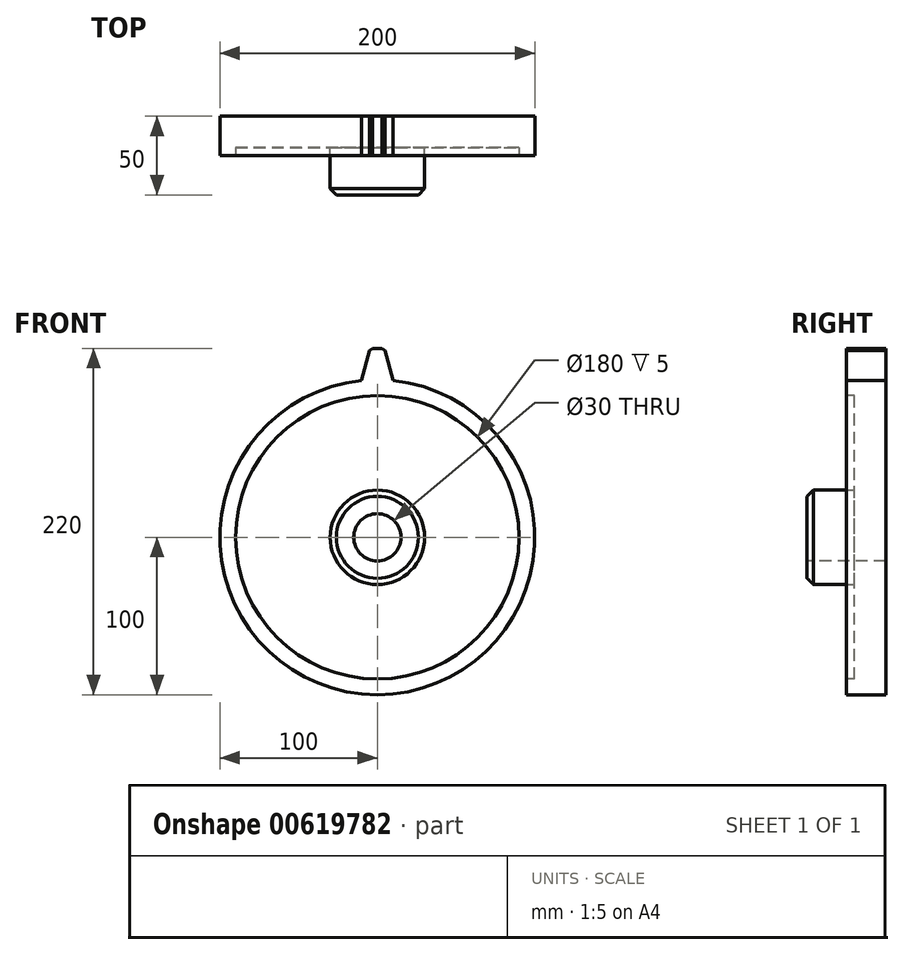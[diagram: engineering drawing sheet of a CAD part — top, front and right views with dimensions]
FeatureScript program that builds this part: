
annotation { "Feature Type Name" : "Feature", "Feature Type Description" : "" }
export const myFeature = defineFeature(function(context is Context, id is Id, definition is map)
    precondition{}
    {
        {
            var Q0;
            Q0=qCreatedBy(makeId("Front.planeOp"),FACE);
            var sketch = newSketch(context, id + "F0", { "sketchPlane" : qUnion([Q0])});
            skCircle(sketch, "E0", {"center": v(0, 0) * mm, "radius": 100 * mm});
            skSolve(sketch);
        }
        {
            var Q0;
            Q0=makeQuery(id+"F0.imprint","IMPRINT",FACE,{"disambiguationData":[TD([[makeQuery(id+"F0.imprint","IMPRINT",EDGE,{"derivedFrom":sQuery(id+"F0.wireOp",EDGE,"E0")}),1.0]])]});
            extrude(context, id + "F1", {"entities" : qUnion([Q0]), "depth" : 25 * mm, "offsetDistance" : 25 * mm});
        }
        {
            var Q0;
            Q0=makeQuery(id+"F1.opExtrude","CAP_FACE",FACE,{"disambiguationData":[OSD([sQuery(id+"F0.wireOp",EDGE,"E0")])],"isStart":false});
            var sketch = newSketch(context, id + "F2", { "sketchPlane" : qUnion([Q0])});
            skLineSegment(sketch, "E1", {"start": v(-10, 99.5) * mm, "end": v(10, 99.5) * mm});
            skLineSegment(sketch, "E2", {"start": v(10, 99.5) * mm, "end": v(4.5, 120) * mm});
            skLineSegment(sketch, "E3", {"start": v(4.5, 120) * mm, "end": v(-4.5, 120) * mm});
            skLineSegment(sketch, "E4", {"start": v(-4.5, 120) * mm, "end": v(-10, 99.5) * mm});
            skSolve(sketch);
        }
        {
            var Q0;
            {var subQ0=sQuery(id+"F2.wireOp",EDGE,"E2");Q0=makeQuery(id+"F2.imprint","IMPRINT",FACE,{"disambiguationData":[TD([[makeQuery(id+"F2.imprint","IMPRINT",EDGE,{"derivedFrom":subQ0}),1.0]])]});}
            var Q1;
            Q1=makeQuery(id+"F1.opExtrude","CAP_FACE",FACE,{"disambiguationData":[OSD([sQuery(id+"F0.wireOp",EDGE,"E0")])],"isStart":true});
            extrude(context, id + "F3", {"entities" : qUnion([Q0]), "operationType" : NewBodyOperationType.ADD, "endBound" : BoundingType.UP_TO_SURFACE, "oppositeDirection" : true, "depth" : 25 * mm, "endBoundEntityFace" : qUnion([Q1]), "offsetDistance" : 25 * mm});
        }
        {
            var Q0;
            Q0=makeQuery(id+"F3.opExtrude","SWEPT_EDGE",EDGE,{"disambiguationData":[OSD([sQuery(id+"F0.wireOp",EDGE,"E0"),sQuery(id+"F2.wireOp",EDGE,"E1"),sQuery(id+"F2.wireOp",EDGE,"E2")])]});
            var Q1;
            Q1=makeQuery(id+"F3.opExtrude","SWEPT_EDGE",EDGE,{"disambiguationData":[OSD([sQuery(id+"F0.wireOp",EDGE,"E0"),sQuery(id+"F2.wireOp",EDGE,"E1"),sQuery(id+"F2.wireOp",EDGE,"E4")])]});
            fillet(context, id + "F4", {"entities" : qUnion([Q0, Q1]), "radius" : 5 * mm, "tangentPropagation" : true, "allowEdgeOverflow" : false});
        }
        {
            var Q0;
            Q0=makeQuery(id+"F3.opExtrude","SWEPT_EDGE",EDGE,{"disambiguationData":[OSD([sQuery(id+"F2.wireOp",EDGE,"E2"),sQuery(id+"F2.wireOp",EDGE,"E3")])]});
            var Q1;
            Q1=makeQuery(id+"F3.opExtrude","SWEPT_EDGE",EDGE,{"disambiguationData":[OSD([sQuery(id+"F2.wireOp",EDGE,"E3"),sQuery(id+"F2.wireOp",EDGE,"E4")])]});
            chamfer(context, id + "F5", {"entities" : qUnion([Q0, Q1]), "width" : 2 * mm, "tangentPropagation" : true});
        }
        {
            var Q0;
            {var subQ0=sQuery(id+"F2.wireOp",EDGE,"E4");var subQ1=sQuery(id+"F2.wireOp",EDGE,"E3");var subQ2=sQuery(id+"F2.wireOp",EDGE,"E2");var subQ3=sQuery(id+"F0.wireOp",EDGE,"E0");Q0=makeQuery(id+"FVngeMlJqadk3JX_1.19.F3.boolean.opBoolean","MERGE",FACE,{"derivedFrom":[makeQuery(id+"FVngeMlJqadk3JX_1.18.F3.boolean.opBoolean","MERGE",FACE,{"derivedFrom":[makeQuery(id+"FVngeMlJqadk3JX_1.17.F3.boolean.opBoolean","MERGE",FACE,{"derivedFrom":[makeQuery(id+"FVngeMlJqadk3JX_1.16.F3.boolean.opBoolean","MERGE",FACE,{"derivedFrom":[makeQuery(id+"FVngeMlJqadk3JX_1.15.F3.boolean.opBoolean","MERGE",FACE,{"derivedFrom":[makeQuery(id+"FVngeMlJqadk3JX_1.14.F3.boolean.opBoolean","MERGE",FACE,{"derivedFrom":[makeQuery(id+"FVngeMlJqadk3JX_1.13.F3.boolean.opBoolean","MERGE",FACE,{"derivedFrom":[makeQuery(id+"FVngeMlJqadk3JX_1.12.F3.boolean.opBoolean","MERGE",FACE,{"derivedFrom":[makeQuery(id+"FVngeMlJqadk3JX_1.11.F3.boolean.opBoolean","MERGE",FACE,{"derivedFrom":[makeQuery(id+"FVngeMlJqadk3JX_1.10.F3.boolean.opBoolean","MERGE",FACE,{"derivedFrom":[makeQuery(id+"FVngeMlJqadk3JX_1.9.F3.boolean.opBoolean","MERGE",FACE,{"derivedFrom":[makeQuery(id+"FVngeMlJqadk3JX_1.8.F3.boolean.opBoolean","MERGE",FACE,{"derivedFrom":[makeQuery(id+"FVngeMlJqadk3JX_1.7.F3.boolean.opBoolean","MERGE",FACE,{"derivedFrom":[makeQuery(id+"FVngeMlJqadk3JX_1.6.F3.boolean.opBoolean","MERGE",FACE,{"derivedFrom":[makeQuery(id+"FVngeMlJqadk3JX_1.5.F3.boolean.opBoolean","MERGE",FACE,{"derivedFrom":[makeQuery(id+"FVngeMlJqadk3JX_1.4.F3.boolean.opBoolean","MERGE",FACE,{"derivedFrom":[makeQuery(id+"FVngeMlJqadk3JX_1.3.F3.boolean.opBoolean","MERGE",FACE,{"derivedFrom":[makeQuery(id+"FVngeMlJqadk3JX_1.2.F3.boolean.opBoolean","MERGE",FACE,{"derivedFrom":[makeQuery(id+"FVngeMlJqadk3JX_1.1.F3.boolean.opBoolean","MERGE",FACE,{"derivedFrom":[makeQuery(id+"F3.boolean.opBoolean","MERGE",FACE,{"derivedFrom":[makeQuery(id+"F1.opExtrude","CAP_FACE",FACE,{"disambiguationData":[OSD([subQ3])],"isStart":false}),makeQuery(id+"F3.opExtrude","CAP_FACE",FACE,{"disambiguationData":[OSD([subQ3,subQ2,subQ1,subQ0])],"isStart":true})]}),makeQuery(id+"FVngeMlJqadk3JX_1.1.F3.opExtrude","CAP_FACE",FACE,{"disambiguationData":[OSD([subQ3,subQ2,subQ1,subQ0])],"isStart":true})]}),makeQuery(id+"FVngeMlJqadk3JX_1.2.F3.opExtrude","CAP_FACE",FACE,{"disambiguationData":[OSD([subQ3,subQ2,subQ1,subQ0])],"isStart":true})]}),makeQuery(id+"FVngeMlJqadk3JX_1.3.F3.opExtrude","CAP_FACE",FACE,{"disambiguationData":[OSD([subQ3,subQ2,subQ1,subQ0])],"isStart":true})]}),makeQuery(id+"FVngeMlJqadk3JX_1.4.F3.opExtrude","CAP_FACE",FACE,{"disambiguationData":[OSD([subQ3,subQ2,subQ1,subQ0])],"isStart":true})]}),makeQuery(id+"FVngeMlJqadk3JX_1.5.F3.opExtrude","CAP_FACE",FACE,{"disambiguationData":[OSD([subQ3,subQ2,subQ1,subQ0])],"isStart":true})]}),makeQuery(id+"FVngeMlJqadk3JX_1.6.F3.opExtrude","CAP_FACE",FACE,{"disambiguationData":[OSD([subQ3,subQ2,subQ1,subQ0])],"isStart":true})]}),makeQuery(id+"FVngeMlJqadk3JX_1.7.F3.opExtrude","CAP_FACE",FACE,{"disambiguationData":[OSD([subQ3,subQ2,subQ1,subQ0])],"isStart":true})]}),makeQuery(id+"FVngeMlJqadk3JX_1.8.F3.opExtrude","CAP_FACE",FACE,{"disambiguationData":[OSD([subQ3,subQ2,subQ1,subQ0])],"isStart":true})]}),makeQuery(id+"FVngeMlJqadk3JX_1.9.F3.opExtrude","CAP_FACE",FACE,{"disambiguationData":[OSD([subQ3,subQ2,subQ1,subQ0])],"isStart":true})]}),makeQuery(id+"FVngeMlJqadk3JX_1.10.F3.opExtrude","CAP_FACE",FACE,{"disambiguationData":[OSD([subQ3,subQ2,subQ1,subQ0])],"isStart":true})]}),makeQuery(id+"FVngeMlJqadk3JX_1.11.F3.opExtrude","CAP_FACE",FACE,{"disambiguationData":[OSD([subQ3,subQ2,subQ1,subQ0])],"isStart":true})]}),makeQuery(id+"FVngeMlJqadk3JX_1.12.F3.opExtrude","CAP_FACE",FACE,{"disambiguationData":[OSD([subQ3,subQ2,subQ1,subQ0])],"isStart":true})]}),makeQuery(id+"FVngeMlJqadk3JX_1.13.F3.opExtrude","CAP_FACE",FACE,{"disambiguationData":[OSD([subQ3,subQ2,subQ1,subQ0])],"isStart":true})]}),makeQuery(id+"FVngeMlJqadk3JX_1.14.F3.opExtrude","CAP_FACE",FACE,{"disambiguationData":[OSD([subQ3,subQ2,subQ1,subQ0])],"isStart":true})]}),makeQuery(id+"FVngeMlJqadk3JX_1.15.F3.opExtrude","CAP_FACE",FACE,{"disambiguationData":[OSD([subQ3,subQ2,subQ1,subQ0])],"isStart":true})]}),makeQuery(id+"FVngeMlJqadk3JX_1.16.F3.opExtrude","CAP_FACE",FACE,{"disambiguationData":[OSD([subQ3,subQ2,subQ1,subQ0])],"isStart":true})]}),makeQuery(id+"FVngeMlJqadk3JX_1.17.F3.opExtrude","CAP_FACE",FACE,{"disambiguationData":[OSD([subQ3,subQ2,subQ1,subQ0])],"isStart":true})]}),makeQuery(id+"FVngeMlJqadk3JX_1.18.F3.opExtrude","CAP_FACE",FACE,{"disambiguationData":[OSD([subQ3,subQ2,subQ1,subQ0])],"isStart":true})]}),makeQuery(id+"FVngeMlJqadk3JX_1.19.F3.opExtrude","CAP_FACE",FACE,{"disambiguationData":[OSD([subQ3,subQ2,subQ1,subQ0])],"isStart":true})]});}
            var sketch = newSketch(context, id + "F6", { "sketchPlane" : qUnion([Q0])});
            skCircle(sketch, "E5", {"center": v(0, 0) * mm, "radius": 90 * mm});
            skSolve(sketch);
        }
        {
            var Q0;
            Q0=makeQuery(id+"F6.imprint","IMPRINT",FACE,{"disambiguationData":[TD([[makeQuery(id+"F6.imprint","IMPRINT",EDGE,{"derivedFrom":sQuery(id+"F6.wireOp",EDGE,"E5")}),1.0]])]});
            extrude(context, id + "F7", {"entities" : qUnion([Q0]), "operationType" : NewBodyOperationType.REMOVE, "oppositeDirection" : true, "depth" : 5 * mm, "offsetDistance" : 25 * mm});
        }
        {
            var Q0;
            Q0=makeQuery(id+"F7.boolean.opBoolean","COPY",FACE,{"derivedFrom":makeQuery(id+"F7.opExtrude","CAP_FACE",FACE,{"disambiguationData":[OSD([sQuery(id+"F6.wireOp",EDGE,"E5")])],"isStart":false})});
            var sketch = newSketch(context, id + "F8", { "sketchPlane" : qUnion([Q0])});
            skCircle(sketch, "E6", {"center": v(0, 0) * mm, "radius": 30 * mm});
            skSolve(sketch);
        }
        {
            var Q0;
            Q0=makeQuery(id+"F8.imprint","IMPRINT",FACE,{"disambiguationData":[TD([[makeQuery(id+"F8.imprint","IMPRINT",EDGE,{"derivedFrom":sQuery(id+"F8.wireOp",EDGE,"E6")}),1.0]])]});
            extrude(context, id + "F9", {"entities" : qUnion([Q0]), "operationType" : NewBodyOperationType.ADD, "depth" : 30 * mm, "offsetDistance" : 25 * mm});
        }
        {
            var Q0;
            Q0=makeQuery(id+"F9.opExtrude","CAP_FACE",FACE,{"disambiguationData":[OSD([sQuery(id+"F8.wireOp",EDGE,"E6")])],"isStart":false});
            var sketch = newSketch(context, id + "F10", { "sketchPlane" : qUnion([Q0])});
            skCircle(sketch, "E7", {"center": v(0, 0) * mm, "radius": 15 * mm});
            skSolve(sketch);
        }
        {
            var Q0;
            Q0=makeQuery(id+"F10.imprint","IMPRINT",FACE,{"disambiguationData":[TD([[makeQuery(id+"F10.imprint","IMPRINT",EDGE,{"derivedFrom":sQuery(id+"F10.wireOp",EDGE,"E7")}),1.0]])]});
            extrude(context, id + "F11", {"entities" : qUnion([Q0]), "operationType" : NewBodyOperationType.REMOVE, "endBound" : BoundingType.THROUGH_ALL, "oppositeDirection" : true, "depth" : 25 * mm, "offsetDistance" : 25 * mm});
        }
        {
            var Q0;
            Q0=makeQuery(id+"F9.opExtrude","CAP_EDGE",EDGE,{"disambiguationData":[OSD([sQuery(id+"F8.wireOp",EDGE,"E6")])],"isStart":false});
            var Q1;
            Q1=makeQuery(id+"F11.boolean.opBoolean","COPY",EDGE,{"derivedFrom":makeQuery(id+"F11.opExtrude","CAP_EDGE",EDGE,{"disambiguationData":[OSD([sQuery(id+"F10.wireOp",EDGE,"E7")])],"isStart":true})});
            chamfer(context, id + "F12", {"entities" : qUnion([Q0, Q1]), "width" : 4 * mm, "tangentPropagation" : true});
        }
    });
